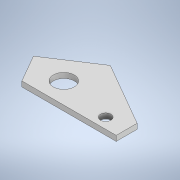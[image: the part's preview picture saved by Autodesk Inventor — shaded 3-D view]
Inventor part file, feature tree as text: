
AUTODESK INVENTOR PART (.ipt)
format: ipt  version: 2022.2 (Build 262287030, 287C)  size: 111,104 bytes
history: native  units: in
note: dims shown in document units (in); Inventor stores cm internally (conversion verified against a paired STEP export)
features: extrude x1, sketch x1
ambient origin geometry x8: Origin, YZ Plane, XZ Plane, XY Plane, X Axis, Y Axis, Z Axis, Center Point
bodies: Solid1 (feature_tree)
feature tree (2):
  extrude  "Extrusion1"  TaperAngle=60.0deg  [1 undecoded]
  sketch  "Sketch1"  dims[d0=60.0deg d1=60.0deg d2=1.0in d3=1.0in d4=1.0in d5=3.5in d6=3.5in d7=4.5in d8=0.5in d9=1.0in d10=0.5in d11=1.5in d12=0.25in d13=0.0in]
note: 1 required parameter value undecoded (feature->parameter linkage not recoverable at this tier; creation-order binding heuristic only, values carry confidence <= 0.55)
